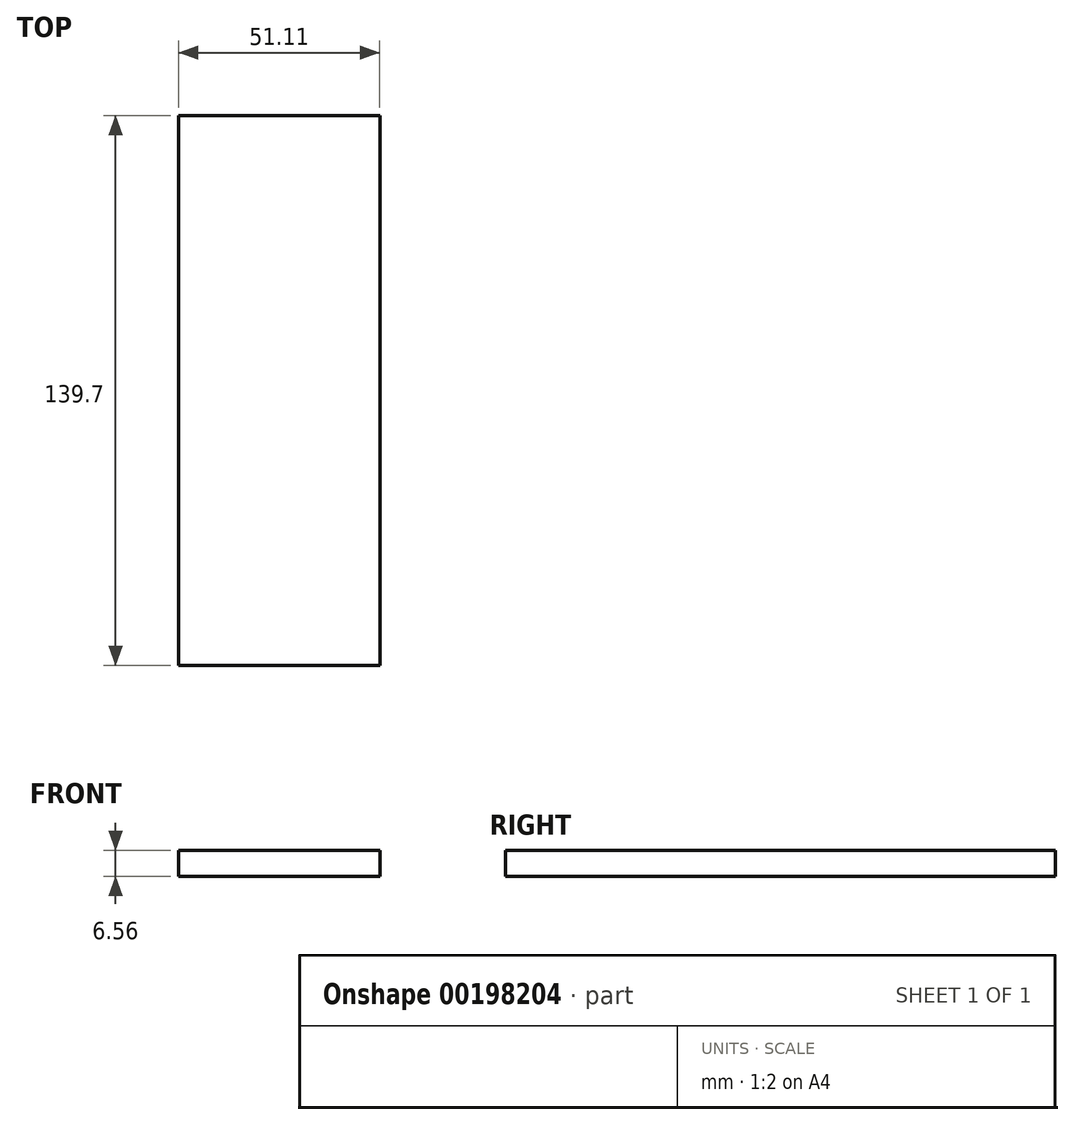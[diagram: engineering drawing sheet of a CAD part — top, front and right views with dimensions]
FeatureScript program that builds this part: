
annotation { "Feature Type Name" : "Feature", "Feature Type Description" : "" }
export const myFeature = defineFeature(function(context is Context, id is Id, definition is map)
    precondition{}
    {
        {
            var Q0;
            Q0=qCreatedBy(makeId("Front.planeOp"),FACE);
            var sketch = newSketch(context, id + "F0", { "sketchPlane" : qUnion([Q0])});
            skLineSegment(sketch, "E0.bottom", {"start": v(0, 0) * mm, "end": v(51.11, 0) * mm});
            skLineSegment(sketch, "E0.top", {"start": v(0, 6.56) * mm, "end": v(51.11, 6.56) * mm});
            skLineSegment(sketch, "E0.left", {"start": v(0, 0) * mm, "end": v(0, 6.56) * mm});
            skLineSegment(sketch, "E0.right", {"start": v(51.11, 0) * mm, "end": v(51.11, 6.56) * mm});
            skSolve(sketch);
        }
        {
            var Q0;
            Q0 = qSketchRegion(id + "F0", true);
            extrude(context, id + "F1", {"entities" : qUnion([Q0]), "depth" : 139.7 * mm});
        }
    });
